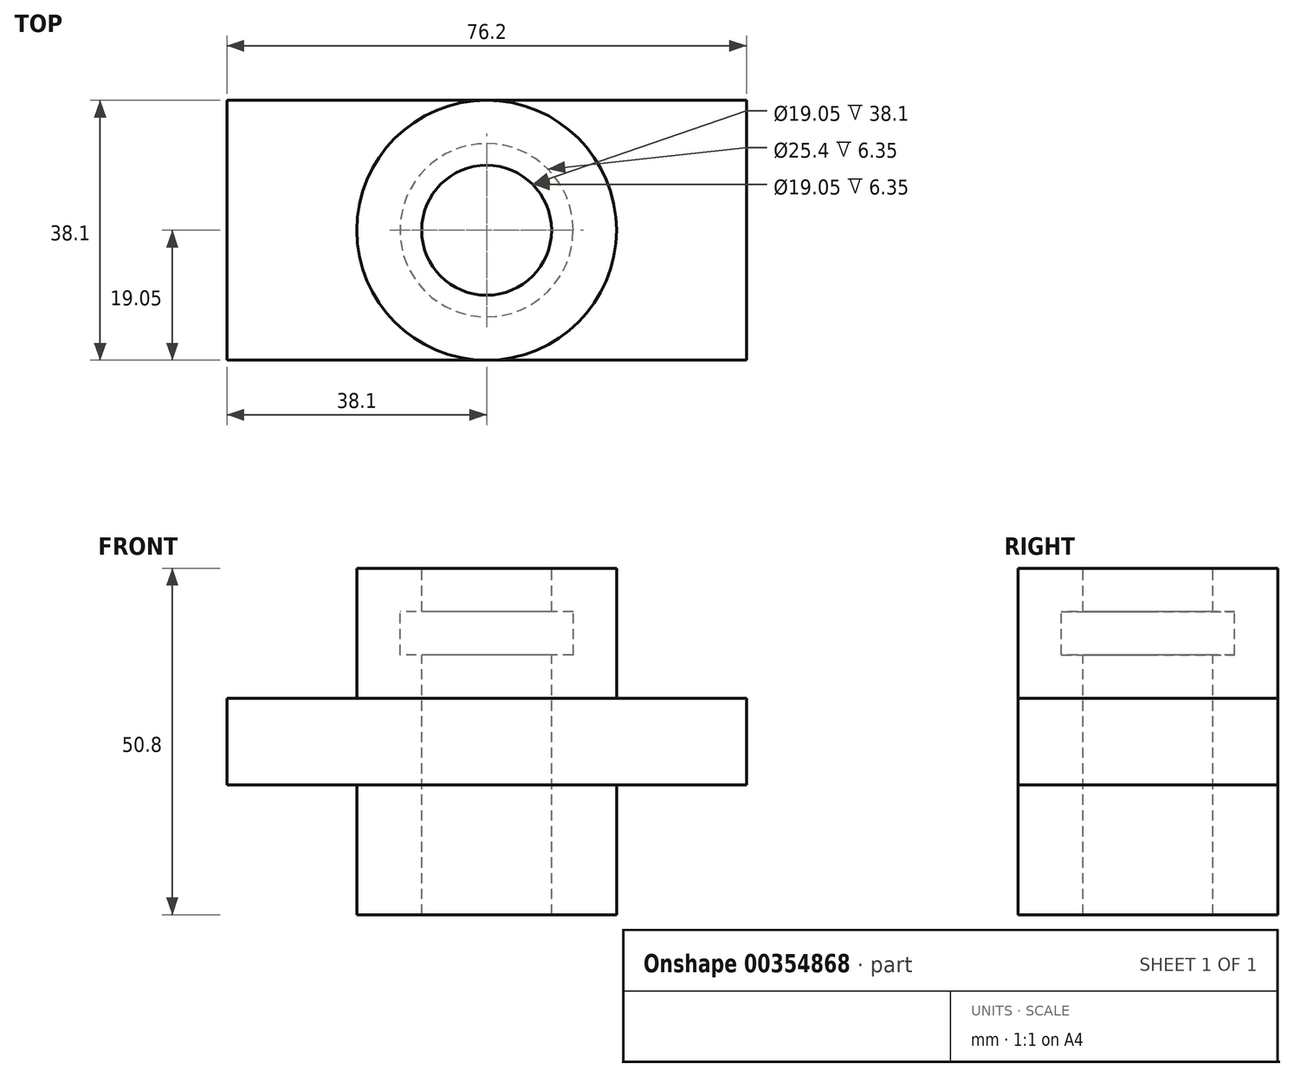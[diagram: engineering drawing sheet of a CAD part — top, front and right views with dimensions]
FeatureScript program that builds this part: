
annotation { "Feature Type Name" : "Feature", "Feature Type Description" : "" }
export const myFeature = defineFeature(function(context is Context, id is Id, definition is map)
    precondition{}
    {
        {
            var Q0;
            Q0=qCreatedBy(makeId("Top.planeOp"),FACE);
            var sketch = newSketch(context, id + "F0", { "sketchPlane" : qUnion([Q0])});
            skCircle(sketch, "E0", {"center": v(0, 0) * mm, "radius": 19.05 * mm});
            skSolve(sketch);
        }
        {
            var Q0;
            Q0=makeQuery(id+"F0.imprint","IMPRINT",FACE,{"disambiguationData":[TD([[makeQuery(id+"F0.imprint","IMPRINT",EDGE,{"derivedFrom":sQuery(id+"F0.wireOp",EDGE,"E0")}),1.0]])]});
            var Q1;
            Q1 = qSketchRegion(id + "FVJKcpGha1Xd14E_1", true);
            extrude(context, id + "F1", {"entities" : qUnion([Q0, Q1]), "endBound" : BoundingType.SYMMETRIC, "depth" : 38.1 * mm});
        }
        {
            var Q0;
            Q0=qCreatedBy(makeId("Top.planeOp"),FACE);
            var sketch = newSketch(context, id + "F2", { "sketchPlane" : qUnion([Q0])});
            skLineSegment(sketch, "E1.bottom", {"start": v(38.1, 19.05) * mm, "end": v(-38.1, 19.05) * mm});
            skLineSegment(sketch, "E1.top", {"start": v(38.1, -19.05) * mm, "end": v(-38.1, -19.05) * mm});
            skLineSegment(sketch, "E1.left", {"start": v(38.1, 19.05) * mm, "end": v(38.1, -19.05) * mm});
            skLineSegment(sketch, "E1.right", {"start": v(-38.1, 19.05) * mm, "end": v(-38.1, -19.05) * mm});
            skPoint(sketch, "E1.middle", {"position": v(0, 0) * mm});
            skSolve(sketch);
        }
        {
            var Q0;
            Q0 = qSketchRegion(id + "F2", true);
            extrude(context, id + "F3", {"entities" : qUnion([Q0]), "operationType" : NewBodyOperationType.ADD, "depth" : 12.7 * mm});
        }
        {
            var Q0;
            Q0=makeQuery(id+"F1.opExtrude","CAP_FACE",FACE,{"disambiguationData":[OSD([sQuery(id+"F0.wireOp",EDGE,"E0")])],"isStart":false});
            var sketch = newSketch(context, id + "F4", { "sketchPlane" : qUnion([Q0])});
            skCircle(sketch, "E2", {"center": v(0, 0) * mm, "radius": 9.53 * mm});
            skSolve(sketch);
        }
        {
            var Q0;
            Q0 = qSketchRegion(id + "F4", true);
            extrude(context, id + "F5", {"entities" : qUnion([Q0]), "operationType" : NewBodyOperationType.REMOVE, "endBound" : BoundingType.THROUGH_ALL, "oppositeDirection" : true, "depth" : 25.4 * mm});
        }
        {
            var Q0;
            Q0=makeQuery(id+"F1.opExtrude","CAP_FACE",FACE,{"disambiguationData":[OSD([sQuery(id+"F0.wireOp",EDGE,"E0")])],"isStart":false});
            var sketch = newSketch(context, id + "F6", { "sketchPlane" : qUnion([Q0])});
            skCircle(sketch, "E3", {"center": v(0, 0) * mm, "radius": 19.05 * mm});
            skSolve(sketch);
        }
        {
            var Q0;
            Q0 = qSketchRegion(id + "F6", true);
            extrude(context, id + "F7", {"entities" : qUnion([Q0]), "operationType" : NewBodyOperationType.ADD, "depth" : 6.35 * mm});
        }
        {
            var Q0;
            Q0=makeQuery(id+"F7.opExtrude","CAP_FACE",FACE,{"disambiguationData":[OSD([sQuery(id+"F6.wireOp",EDGE,"E3")])],"isStart":false});
            var sketch = newSketch(context, id + "F8", { "sketchPlane" : qUnion([Q0])});
            skCircle(sketch, "E4", {"center": v(0, 0) * mm, "radius": 12.7 * mm});
            skSolve(sketch);
        }
        {
            var Q0;
            Q0 = qSketchRegion(id + "F8", true);
            extrude(context, id + "F9", {"entities" : qUnion([Q0]), "operationType" : NewBodyOperationType.REMOVE, "oppositeDirection" : true, "depth" : 6.35 * mm});
        }
        {
            var Q0;
            Q0=makeQuery(id+"F7.opExtrude","CAP_FACE",FACE,{"disambiguationData":[OSD([sQuery(id+"F6.wireOp",EDGE,"E3")])],"isStart":false});
            var sketch = newSketch(context, id + "F10", { "sketchPlane" : qUnion([Q0])});
            skCircle(sketch, "E5", {"center": v(0, 0) * mm, "radius": 19.05 * mm});
            skSolve(sketch);
        }
        {
            var Q0;
            Q0 = qSketchRegion(id + "F10", true);
            extrude(context, id + "F11", {"entities" : qUnion([Q0]), "operationType" : NewBodyOperationType.ADD, "depth" : 6.35 * mm});
        }
        {
            var Q0;
            Q0=makeQuery(id+"F11.opExtrude","CAP_FACE",FACE,{"disambiguationData":[OSD([sQuery(id+"F10.wireOp",EDGE,"E5")])],"isStart":false});
            var sketch = newSketch(context, id + "F12", { "sketchPlane" : qUnion([Q0])});
            skCircle(sketch, "E6", {"center": v(0, 0) * mm, "radius": 9.53 * mm});
            skSolve(sketch);
        }
        {
            var Q0;
            Q0 = qSketchRegion(id + "F12", true);
            extrude(context, id + "F13", {"entities" : qUnion([Q0]), "operationType" : NewBodyOperationType.REMOVE, "oppositeDirection" : true, "depth" : 6.35 * mm});
        }
    });
